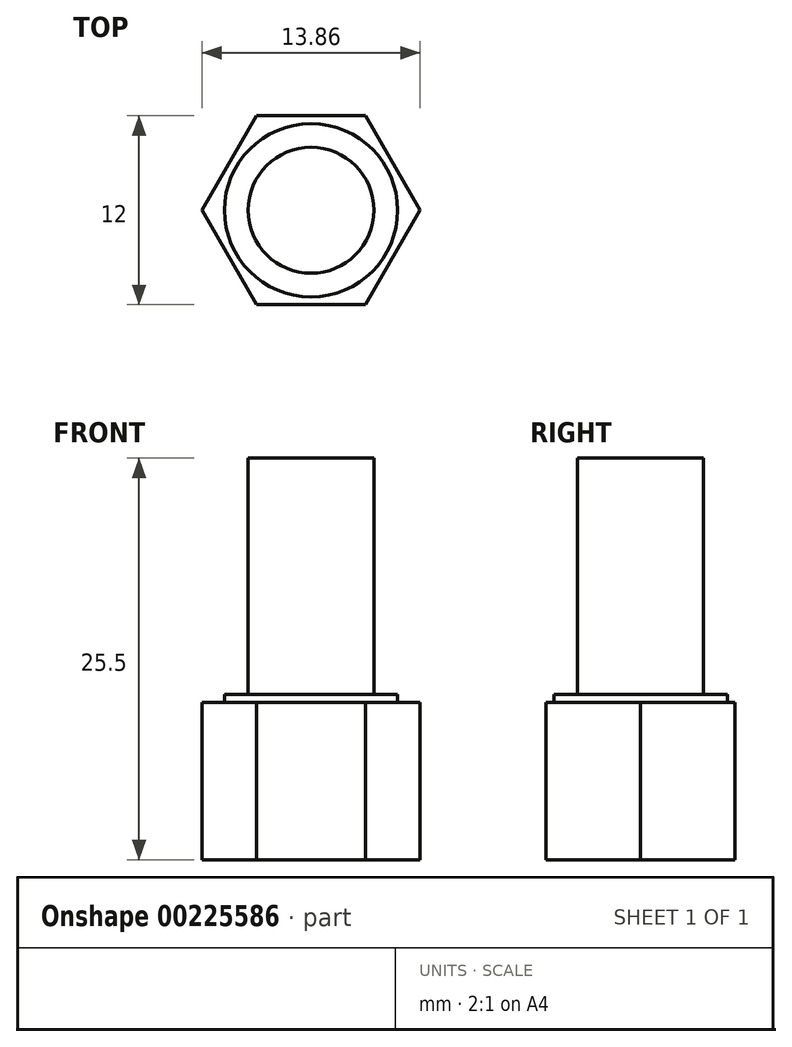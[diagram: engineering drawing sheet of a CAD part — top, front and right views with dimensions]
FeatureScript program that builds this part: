
annotation { "Feature Type Name" : "Feature", "Feature Type Description" : "" }
export const myFeature = defineFeature(function(context is Context, id is Id, definition is map)
    precondition{}
    {
        {
            var Q0;
            Q0=qCreatedBy(makeId("Top.planeOp"),FACE);
            var sketch = newSketch(context, id + "F0", { "sketchPlane" : qUnion([Q0])});
            skCircle(sketch, "E0.cCircle", {"center": v(0, 0) * mm, "radius": 6 * mm, "construction": true});
            skLineSegment(sketch, "E0.0", {"start": v(-3.46, 6) * mm, "end": v(3.46, 6) * mm});
            skLineSegment(sketch, "E0.1", {"start": v(3.46, 6) * mm, "end": v(6.93, 0) * mm});
            skLineSegment(sketch, "E0.2", {"start": v(6.93, 0) * mm, "end": v(3.46, -6) * mm});
            skLineSegment(sketch, "E0.3", {"start": v(3.46, -6) * mm, "end": v(-3.46, -6) * mm});
            skLineSegment(sketch, "E0.4", {"start": v(-3.46, -6) * mm, "end": v(-6.93, 0) * mm});
            skLineSegment(sketch, "E0.5", {"start": v(-6.93, 0) * mm, "end": v(-3.46, 6) * mm});
            skPoint(sketch, "E0.0.midPoint", {"position": v(0, 6) * mm});
            skSolve(sketch);
        }
        {
            var Q0;
            Q0=makeQuery(id+"F0.imprint","IMPRINT",FACE,{"disambiguationData":[TD([[makeQuery(id+"F0.imprint","IMPRINT",EDGE,{"derivedFrom":sQuery(id+"F0.wireOp",EDGE,"E0.0")}),-1.0]])]});
            extrude(context, id + "F1", {"entities" : qUnion([Q0]), "depth" : 10 * mm});
        }
        {
            var Q0;
            Q0=makeQuery(id+"F1.opExtrude","CAP_FACE",FACE,{"disambiguationData":[OSD([sQuery(id+"F0.wireOp",EDGE,"E0.0"),sQuery(id+"F0.wireOp",EDGE,"E0.1"),sQuery(id+"F0.wireOp",EDGE,"E0.2"),sQuery(id+"F0.wireOp",EDGE,"E0.3"),sQuery(id+"F0.wireOp",EDGE,"E0.4"),sQuery(id+"F0.wireOp",EDGE,"E0.5")])],"isStart":false});
            var sketch = newSketch(context, id + "F2", { "sketchPlane" : qUnion([Q0])});
            skCircle(sketch, "E1", {"center": v(0, 0) * mm, "radius": 5.5 * mm});
            skSolve(sketch);
        }
        {
            var Q0;
            Q0=makeQuery(id+"F2.imprint","IMPRINT",FACE,{"disambiguationData":[TD([[makeQuery(id+"F2.imprint","IMPRINT",EDGE,{"derivedFrom":sQuery(id+"F2.wireOp",EDGE,"E1")}),1.0]])]});
            extrude(context, id + "F3", {"entities" : qUnion([Q0]), "operationType" : NewBodyOperationType.ADD, "depth" : 0.5 * mm});
        }
        {
            var Q0;
            Q0=makeQuery(id+"F3.opExtrude","CAP_FACE",FACE,{"disambiguationData":[OSD([sQuery(id+"F2.wireOp",EDGE,"E1")])],"isStart":false});
            var sketch = newSketch(context, id + "F4", { "sketchPlane" : qUnion([Q0])});
            skCircle(sketch, "E2", {"center": v(0, 0) * mm, "radius": 4 * mm});
            skSolve(sketch);
        }
        {
            var Q0;
            Q0=makeQuery(id+"F4.imprint","IMPRINT",FACE,{"disambiguationData":[TD([[makeQuery(id+"F4.imprint","IMPRINT",EDGE,{"derivedFrom":sQuery(id+"F4.wireOp",EDGE,"E2")}),1.0]])]});
            extrude(context, id + "F5", {"entities" : qUnion([Q0]), "operationType" : NewBodyOperationType.ADD, "depth" : 15 * mm});
        }
    });
